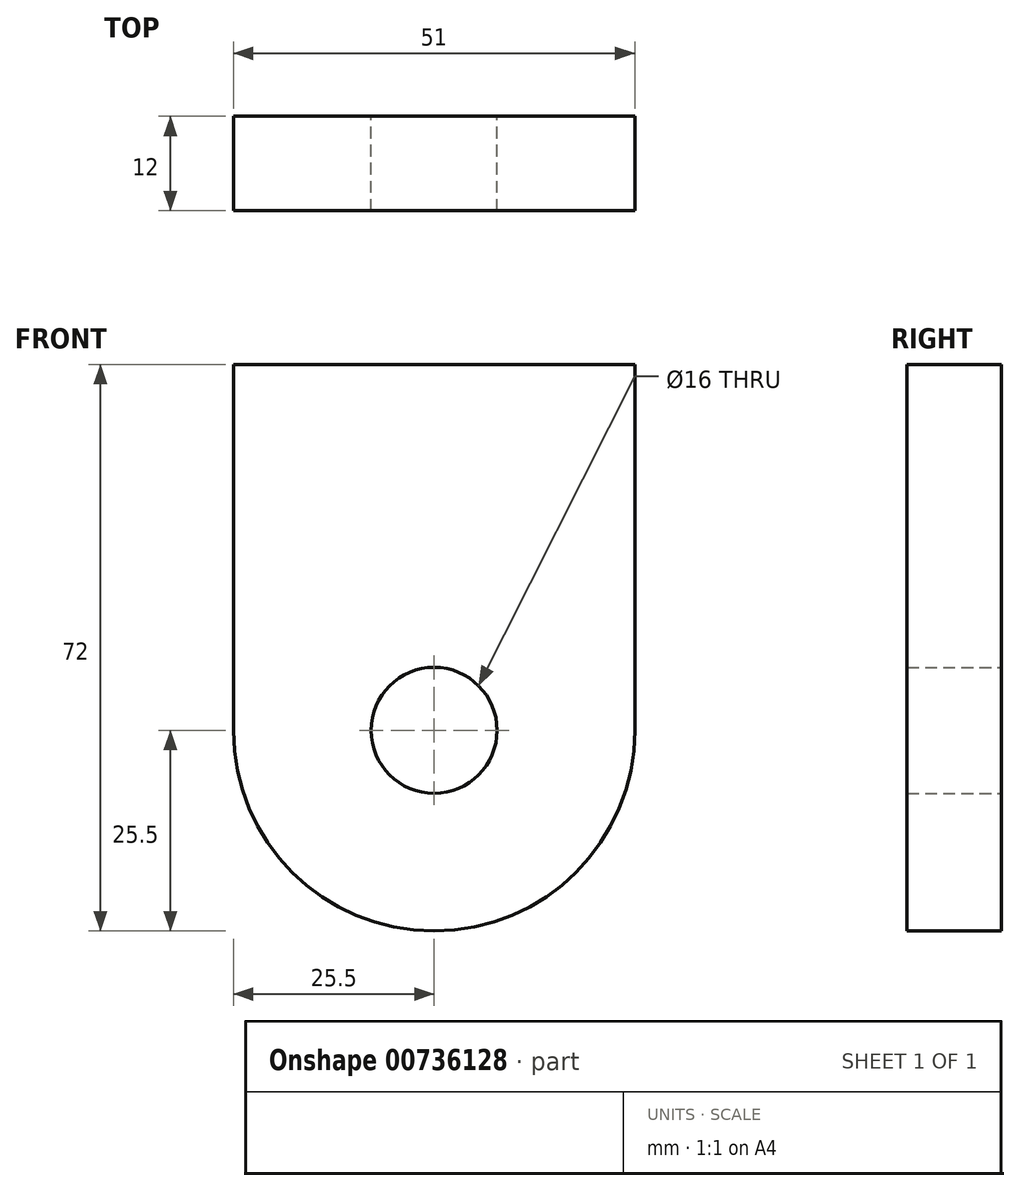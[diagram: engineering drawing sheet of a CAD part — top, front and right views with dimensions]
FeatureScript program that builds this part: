
annotation { "Feature Type Name" : "Feature", "Feature Type Description" : "" }
export const myFeature = defineFeature(function(context is Context, id is Id, definition is map)
    precondition{}
    {
        {
            var Q0;
            Q0=qCreatedBy(makeId("Front.planeOp"),FACE);
            var sketch = newSketch(context, id + "F0", { "sketchPlane" : qUnion([Q0])});
            skLineSegment(sketch, "E0.bottom", {"start": v(-25.5, 36) * mm, "end": v(25.5, 36) * mm});
            skLineSegment(sketch, "E0.left", {"start": v(-25.5, 36) * mm, "end": v(-25.5, -10.5) * mm});
            skLineSegment(sketch, "E0.right", {"start": v(25.5, 36) * mm, "end": v(25.5, -10.5) * mm});
            skPoint(sketch, "E0.middle", {"position": v(0, 0) * mm});
            skArc(sketch, "E1", {"start": v(-25.5, -10.5) * mm, "mid": v(0, -36) * mm, "end": v(25.5, -10.5) * mm});
            skPoint(sketch, "E2", {"position": v(0, -36) * mm});
            skCircle(sketch, "E3", {"center": v(0, -10.5) * mm, "radius": 8 * mm});
            skSolve(sketch);
        }
        {
            var Q0;
            Q0=makeQuery(id+"F0.imprint","IMPRINT",FACE,{"disambiguationData":[TD([[makeQuery(id+"F0.imprint","IMPRINT",EDGE,{"derivedFrom":sQuery(id+"F0.wireOp",EDGE,"E0.bottom")}),-1.0]])]});
            extrude(context, id + "F1", {"entities" : qUnion([Q0]), "depth" : 12 * mm, "offsetDistance" : 25 * mm});
        }
    });
